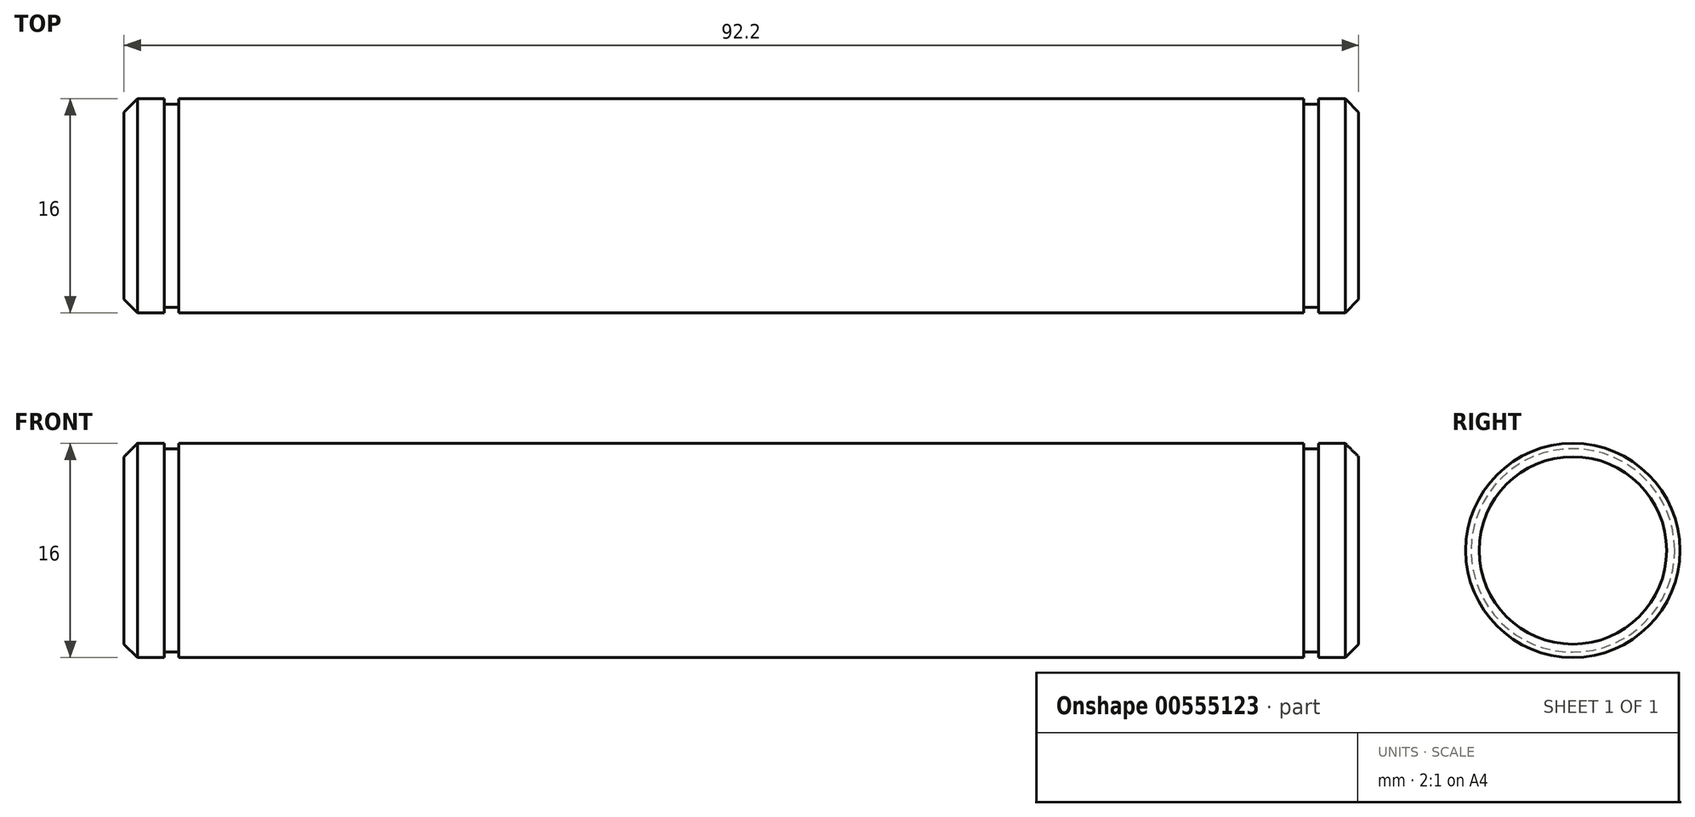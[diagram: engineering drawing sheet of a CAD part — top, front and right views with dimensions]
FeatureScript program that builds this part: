
annotation { "Feature Type Name" : "Feature", "Feature Type Description" : "" }
export const myFeature = defineFeature(function(context is Context, id is Id, definition is map)
    precondition{}
    {
        {
            var Q0;
            Q0=qCreatedBy(makeId("Front.planeOp"),FACE);
            var sketch = newSketch(context, id + "F0", { "sketchPlane" : qUnion([Q0])});
            skLineSegment(sketch, "E0.top", {"start": v(0, 8) * mm, "end": v(-42, 8) * mm});
            skLineSegment(sketch, "E0.right", {"start": v(-46.1, 0) * mm, "end": v(-46.1, 8) * mm});
            skLineSegment(sketch, "E1.top", {"start": v(-43.1, 7.6) * mm, "end": v(-42, 7.6) * mm});
            skLineSegment(sketch, "E1.left", {"start": v(-43.1, 8) * mm, "end": v(-43.1, 7.6) * mm});
            skLineSegment(sketch, "E1.right", {"start": v(-42, 8) * mm, "end": v(-42, 7.6) * mm});
            skLineSegment(sketch, "E2.trimOffspring", {"start": v(-43.1, 8) * mm, "end": v(-46.1, 8) * mm});
            skLineSegment(sketch, "E3.MirrorCS", {"start": v(43.1, 7.6) * mm, "end": v(42, 7.6) * mm});
            skLineSegment(sketch, "E4.MirrorCS", {"start": v(43.1, 8) * mm, "end": v(43.1, 7.6) * mm});
            skLineSegment(sketch, "E5.MirrorCS", {"start": v(42, 8) * mm, "end": v(42, 7.6) * mm});
            skLineSegment(sketch, "E6.MirrorCS", {"start": v(0, 8) * mm, "end": v(42, 8) * mm});
            skLineSegment(sketch, "E7.MirrorCS", {"start": v(43.1, 8) * mm, "end": v(46.1, 8) * mm});
            skLineSegment(sketch, "E8.MirrorCS", {"start": v(46.1, 0) * mm, "end": v(46.1, 8) * mm});
            skLineSegment(sketch, "E9.MirrorCS", {"start": v(-43.1, -8) * mm, "end": v(-43.1, -7.6) * mm});
            skLineSegment(sketch, "E10.MirrorCS", {"start": v(-42, -8) * mm, "end": v(-42, -7.6) * mm});
            skLineSegment(sketch, "E11.MirrorCS", {"start": v(-43.1, -7.6) * mm, "end": v(-42, -7.6) * mm});
            skLineSegment(sketch, "E12.MirrorCS", {"start": v(42, -8) * mm, "end": v(42, -7.6) * mm});
            skLineSegment(sketch, "E13.MirrorCS", {"start": v(43.1, -8) * mm, "end": v(43.1, -7.6) * mm});
            skLineSegment(sketch, "E14.MirrorCS", {"start": v(43.1, -7.6) * mm, "end": v(42, -7.6) * mm});
            skLineSegment(sketch, "E15.MirrorCS", {"start": v(46.1, 0) * mm, "end": v(46.1, -8) * mm});
            skLineSegment(sketch, "E16.MirrorCS", {"start": v(43.1, -8) * mm, "end": v(46.1, -8) * mm});
            skLineSegment(sketch, "E17.MirrorCS", {"start": v(0, -8) * mm, "end": v(42, -8) * mm});
            skLineSegment(sketch, "E18.MirrorCS", {"start": v(-43.1, -8) * mm, "end": v(-46.1, -8) * mm});
            skLineSegment(sketch, "E19.MirrorCS", {"start": v(0, -8) * mm, "end": v(-42, -8) * mm});
            skLineSegment(sketch, "E20.MirrorCS", {"start": v(-46.1, 0) * mm, "end": v(-46.1, -8) * mm});
            skPoint(sketch, "E0.left.start.orphan", {"position": v(0, 0) * mm});
            skLineSegment(sketch, "E21", {"start": v(-46.1, 0) * mm, "end": v(46.1, 0) * mm});
            skSolve(sketch);
        }
        {
            var Q0;
            Q0=makeQuery(id+"F0.imprint","IMPRINT",FACE,{"disambiguationData":[TD([[makeQuery(id+"F0.imprint","IMPRINT",EDGE,{"derivedFrom":sQuery(id+"F0.wireOp",EDGE,"E0.top")}),1.0]])]});
            var Q1;
            Q1=sQuery(id+"F0.wireOp",EDGE,"E21");
            revolve(context, id + "F1", {"entities" : qUnion([Q0]), "axis" : qUnion([Q1]), "revolveType" : RevolveType.FULL});
        }
        {
            var Q0;
            Q0=makeQuery(id+"F1.opRevolve","SWEPT_EDGE",EDGE,{"disambiguationData":[OSD([sQuery(id+"F0.wireOp",EDGE,"E0.right"),sQuery(id+"F0.wireOp",EDGE,"E2.trimOffspring")])]});
            var Q1;
            Q1=makeQuery(id+"F1.opRevolve","SWEPT_EDGE",EDGE,{"disambiguationData":[OSD([sQuery(id+"F0.wireOp",EDGE,"E7.MirrorCS"),sQuery(id+"F0.wireOp",EDGE,"E8.MirrorCS")])]});
            chamfer(context, id + "F2", {"entities" : qUnion([Q0, Q1]), "width" : 1 * mm, "tangentPropagation" : true});
        }
    });
